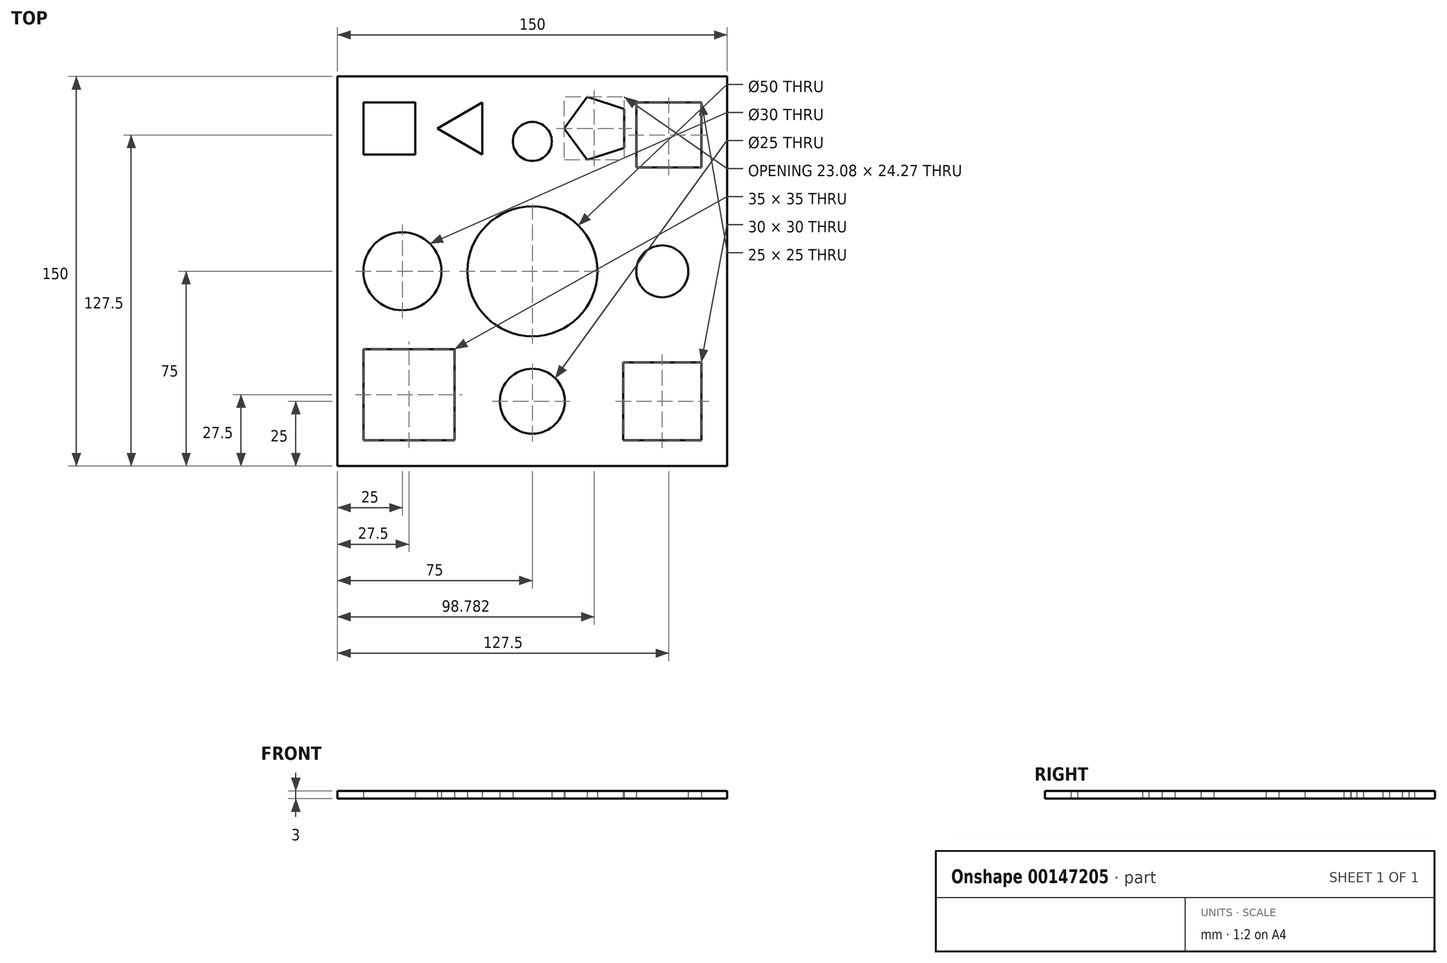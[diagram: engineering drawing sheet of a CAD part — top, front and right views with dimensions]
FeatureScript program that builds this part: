
annotation { "Feature Type Name" : "Feature", "Feature Type Description" : "" }
export const myFeature = defineFeature(function(context is Context, id is Id, definition is map)
    precondition{}
    {
        {
            var Q0;
            Q0=qCreatedBy(makeId("Top.planeOp"),FACE);
            var sketch = newSketch(context, id + "F0", { "sketchPlane" : qUnion([Q0])});
            skLineSegment(sketch, "E0.bottom", {"start": v(0, 0) * mm, "end": v(150, 0) * mm});
            skLineSegment(sketch, "E0.top", {"start": v(0, -150) * mm, "end": v(150, -150) * mm});
            skLineSegment(sketch, "E0.left", {"start": v(0, 0) * mm, "end": v(0, -150) * mm});
            skLineSegment(sketch, "E0.right", {"start": v(150, 0) * mm, "end": v(150, -150) * mm});
            skLineSegment(sketch, "E1", {"start": v(0, -75) * mm, "end": v(164.27, -75) * mm, "construction": true});
            skPoint(sketch, "E1.endSnap0", {"position": v(150, -75) * mm});
            skLineSegment(sketch, "E2", {"start": v(75, 0) * mm, "end": v(75, -169.44) * mm, "construction": true});
            skCircle(sketch, "E3", {"center": v(75, -75) * mm, "radius": 25 * mm});
            skCircle(sketch, "E4", {"center": v(75, -25) * mm, "radius": 7.5 * mm});
            skCircle(sketch, "E5", {"center": v(125, -75) * mm, "radius": 10 * mm});
            skCircle(sketch, "E6", {"center": v(25, -75) * mm, "radius": 15 * mm});
            skCircle(sketch, "E7", {"center": v(75, -125) * mm, "radius": 12.5 * mm});
            skLineSegment(sketch, "E8.bottom", {"start": v(10, -10) * mm, "end": v(30, -10) * mm});
            skLineSegment(sketch, "E8.top", {"start": v(10, -30) * mm, "end": v(30, -30) * mm});
            skLineSegment(sketch, "E8.left", {"start": v(10, -10) * mm, "end": v(10, -30) * mm});
            skLineSegment(sketch, "E8.right", {"start": v(30, -10) * mm, "end": v(30, -30) * mm});
            skLineSegment(sketch, "E9.bottom", {"start": v(115, -10) * mm, "end": v(140, -10) * mm});
            skLineSegment(sketch, "E9.top", {"start": v(115, -35) * mm, "end": v(140, -35) * mm});
            skLineSegment(sketch, "E9.left", {"start": v(115, -10) * mm, "end": v(115, -35) * mm});
            skLineSegment(sketch, "E9.right", {"start": v(140, -10) * mm, "end": v(140, -35) * mm});
            skLineSegment(sketch, "E10.bottom", {"start": v(110, -110) * mm, "end": v(140, -110) * mm});
            skLineSegment(sketch, "E10.top", {"start": v(110, -140) * mm, "end": v(140, -140) * mm});
            skLineSegment(sketch, "E10.left", {"start": v(110, -110) * mm, "end": v(110, -140) * mm});
            skLineSegment(sketch, "E10.right", {"start": v(140, -110) * mm, "end": v(140, -140) * mm});
            skLineSegment(sketch, "E11.bottom", {"start": v(10, -105) * mm, "end": v(45, -105) * mm});
            skLineSegment(sketch, "E11.top", {"start": v(10, -140) * mm, "end": v(45, -140) * mm});
            skLineSegment(sketch, "E11.left", {"start": v(10, -105) * mm, "end": v(10, -140) * mm});
            skLineSegment(sketch, "E11.right", {"start": v(45, -105) * mm, "end": v(45, -140) * mm});
            skCircle(sketch, "E12.cCircle", {"center": v(50, -20) * mm, "radius": 5.77 * mm, "construction": true});
            skLineSegment(sketch, "E12.0", {"start": v(55.77, -10) * mm, "end": v(55.77, -30) * mm});
            skLineSegment(sketch, "E12.1", {"start": v(55.77, -30) * mm, "end": v(38.45, -20) * mm});
            skLineSegment(sketch, "E12.2", {"start": v(38.45, -20) * mm, "end": v(55.77, -10) * mm});
            skPoint(sketch, "E12.0.midPoint", {"position": v(55.77, -20) * mm});
            skCircle(sketch, "E13.cCircle", {"center": v(100, -20) * mm, "radius": 10.32 * mm, "construction": true});
            skLineSegment(sketch, "E13.0", {"start": v(110.32, -12.5) * mm, "end": v(110.32, -27.5) * mm});
            skLineSegment(sketch, "E13.1", {"start": v(110.32, -27.5) * mm, "end": v(96.06, -32.14) * mm});
            skLineSegment(sketch, "E13.2", {"start": v(96.06, -32.14) * mm, "end": v(87.24, -20) * mm});
            skLineSegment(sketch, "E13.3", {"start": v(87.24, -20) * mm, "end": v(96.06, -7.86) * mm});
            skLineSegment(sketch, "E13.4", {"start": v(96.06, -7.86) * mm, "end": v(110.32, -12.5) * mm});
            skPoint(sketch, "E13.0.midPoint", {"position": v(110.32, -20) * mm});
            skSolve(sketch);
        }
        {
            var Q0;
            Q0 = qSketchRegion(id + "F0", true);
            extrude(context, id + "F1", {"entities" : qUnion([Q0]), "depth" : 3 * mm});
        }
    });
